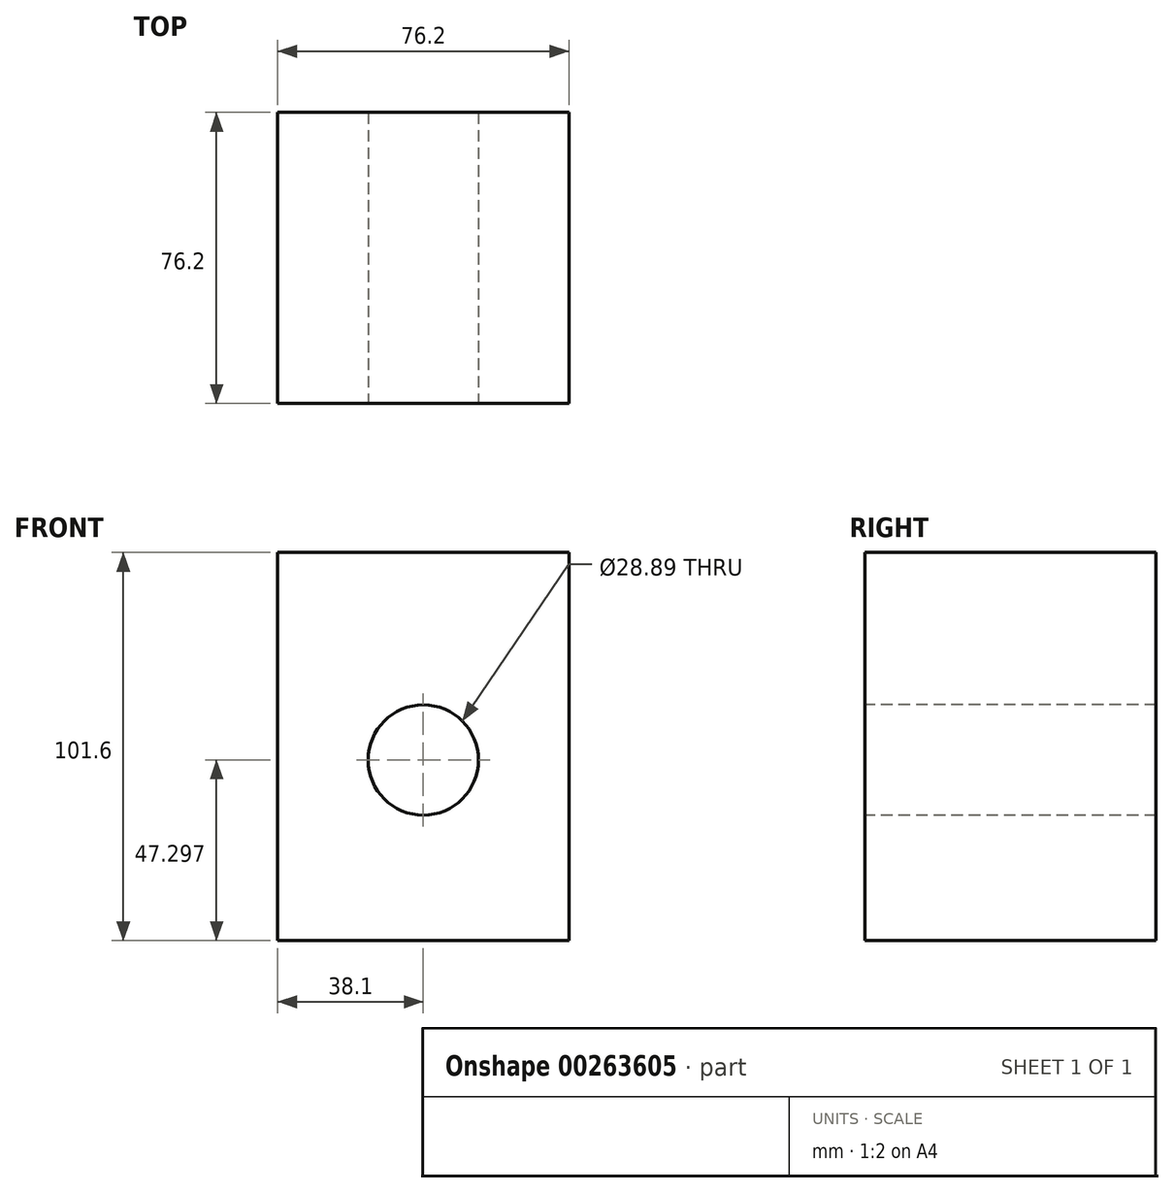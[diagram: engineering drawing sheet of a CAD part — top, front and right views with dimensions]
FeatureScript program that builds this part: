
annotation { "Feature Type Name" : "Feature", "Feature Type Description" : "" }
export const myFeature = defineFeature(function(context is Context, id is Id, definition is map)
    precondition{}
    {
        {
            var Q0;
            Q0=qCreatedBy(makeId("Front.planeOp"),FACE);
            var sketch = newSketch(context, id + "F0", { "sketchPlane" : qUnion([Q0])});
            skLineSegment(sketch, "E0.bottom", {"start": v(0, 0) * mm, "end": v(76.2, 0) * mm});
            skLineSegment(sketch, "E0.top", {"start": v(0, 101.6) * mm, "end": v(76.2, 101.6) * mm});
            skLineSegment(sketch, "E0.left", {"start": v(0, 0) * mm, "end": v(0, 101.6) * mm});
            skLineSegment(sketch, "E0.right", {"start": v(76.2, 0) * mm, "end": v(76.2, 101.6) * mm});
            skSolve(sketch);
        }
        {
            var Q0;
            Q0=makeQuery(id+"F0.imprint","IMPRINT",FACE,{"disambiguationData":[TD([[makeQuery(id+"F0.imprint","IMPRINT",EDGE,{"derivedFrom":sQuery(id+"F0.wireOp",EDGE,"E0.bottom")}),1.0]])]});
            extrude(context, id + "F1", {"entities" : qUnion([Q0]), "oppositeDirection" : true, "depth" : 76.2 * mm});
        }
        {
            var Q0;
            Q0=makeQuery(id+"F1.opExtrude","CAP_FACE",FACE,{"disambiguationData":[OSD([sQuery(id+"F0.wireOp",EDGE,"E0.bottom"),sQuery(id+"F0.wireOp",EDGE,"E0.top"),sQuery(id+"F0.wireOp",EDGE,"E0.left"),sQuery(id+"F0.wireOp",EDGE,"E0.right")])],"isStart":true});
            var sketch = newSketch(context, id + "F2", { "sketchPlane" : qUnion([Q0])});
            skCircle(sketch, "E1", {"center": v(38.1, 47.3) * mm, "radius": 14.44 * mm});
            skPoint(sketch, "E1.centerSnap0", {"position": v(38.1, 0) * mm});
            skSolve(sketch);
        }
        {
            var Q0;
            Q0=makeQuery(id+"F2.imprint","IMPRINT",FACE,{"disambiguationData":[TD([[makeQuery(id+"F2.imprint","IMPRINT",EDGE,{"derivedFrom":sQuery(id+"F2.wireOp",EDGE,"E1")}),1.0]])]});
            extrude(context, id + "F3", {"entities" : qUnion([Q0]), "operationType" : NewBodyOperationType.REMOVE, "oppositeDirection" : true, "depth" : 76.2 * mm});
        }
    });
